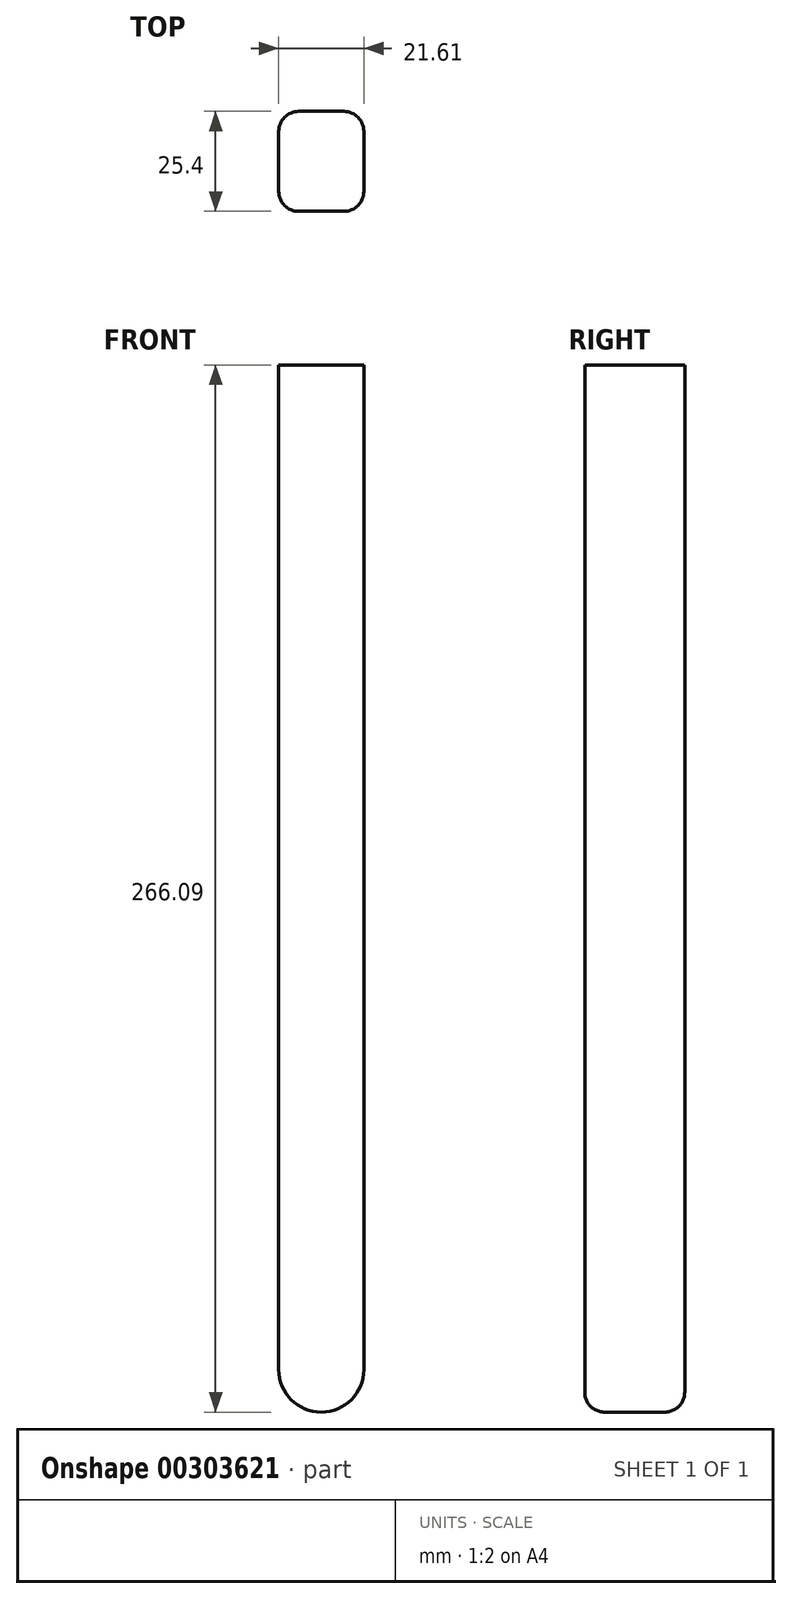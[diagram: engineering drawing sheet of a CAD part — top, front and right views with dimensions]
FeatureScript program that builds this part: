
annotation { "Feature Type Name" : "Feature", "Feature Type Description" : "" }
export const myFeature = defineFeature(function(context is Context, id is Id, definition is map)
    precondition{}
    {
        {
            var Q0;
            Q0=qCreatedBy(makeId("Front.planeOp"),FACE);
            var sketch = newSketch(context, id + "F0", { "sketchPlane" : qUnion([Q0])});
            skArc(sketch, "E0", {"start": v(-36.96, -36.2) * mm, "mid": v(-26.15, -47) * mm, "end": v(-15.35, -36.2) * mm});
            skLineSegment(sketch, "E1", {"start": v(-15.35, -36.2) * mm, "end": v(-15.35, 219.08) * mm});
            skLineSegment(sketch, "E2", {"start": v(-36.96, -36.2) * mm, "end": v(-36.96, 219.08) * mm});
            skLineSegment(sketch, "E3", {"start": v(-36.96, 219.08) * mm, "end": v(-15.35, 219.08) * mm});
            skSolve(sketch);
        }
        {
            var Q0;
            Q0 = qSketchRegion(id + "F0", true);
            extrude(context, id + "F1", {"entities" : qUnion([Q0]), "depth" : 25.4 * mm});
        }
        {
            var Q0;
            Q0=makeQuery(id+"F1.opExtrude","SWEPT_FACE",FACE,{"disambiguationData":[OSD([sQuery(id+"F0.wireOp",EDGE,"E0")])]});
            fillet(context, id + "F2", {"entities" : qUnion([Q0]), "radius" : 5.08 * mm, "tangentPropagation" : true, "allowEdgeOverflow" : false});
        }
    });
